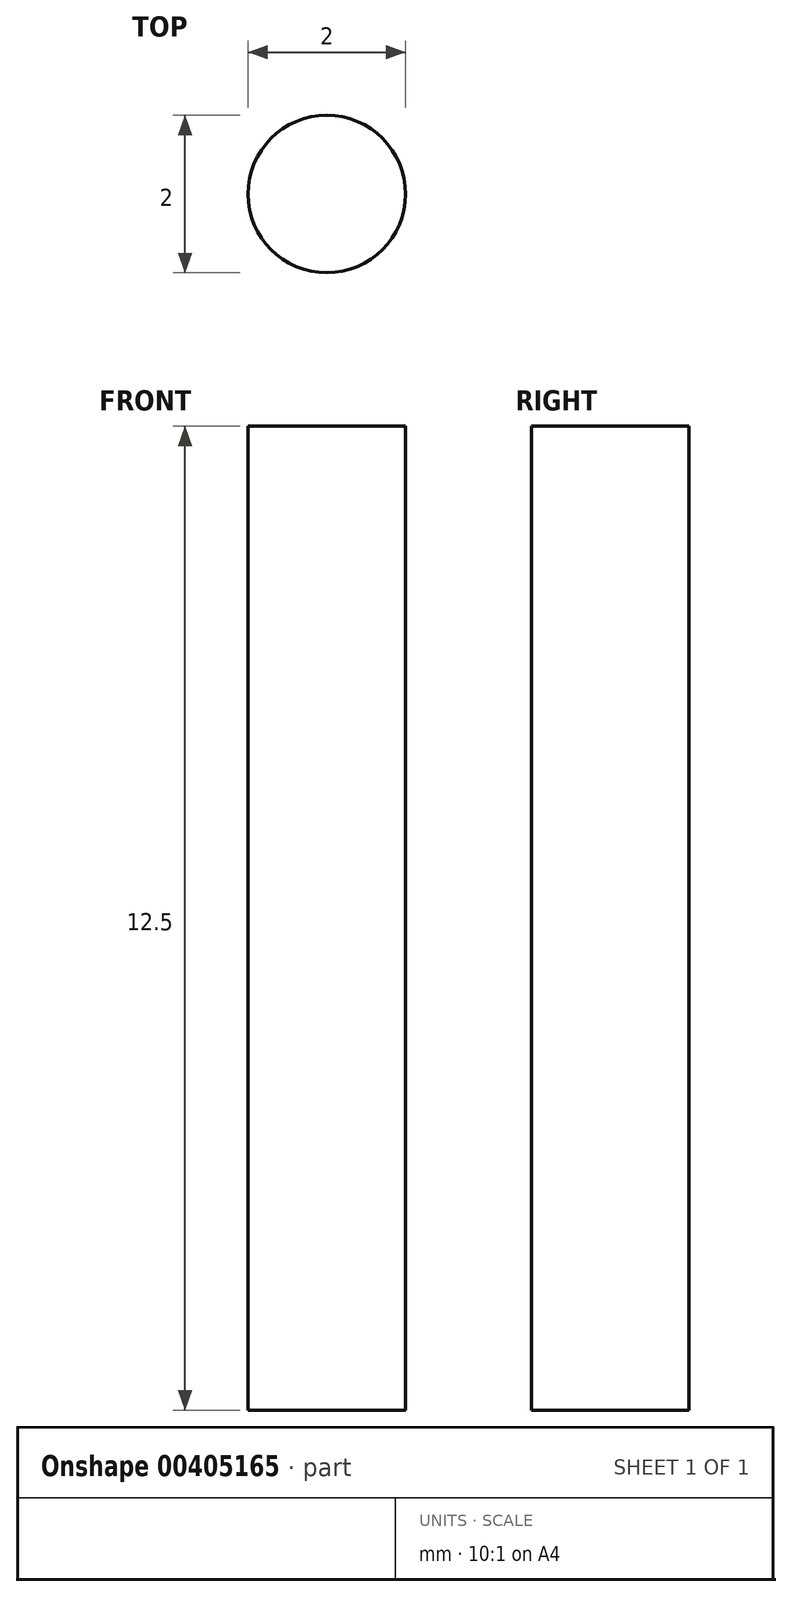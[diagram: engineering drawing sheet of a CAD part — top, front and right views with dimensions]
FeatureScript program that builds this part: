
annotation { "Feature Type Name" : "Feature", "Feature Type Description" : "" }
export const myFeature = defineFeature(function(context is Context, id is Id, definition is map)
    precondition{}
    {
        {
            var Q0;
            Q0=qCreatedBy(makeId("Top.planeOp"),FACE);
            var sketch = newSketch(context, id + "F0", { "sketchPlane" : qUnion([Q0])});
            skCircle(sketch, "E0", {"center": v(0, 0) * mm, "radius": 1 * mm});
            skSolve(sketch);
        }
        {
            var Q0;
            Q0 = qSketchRegion(id + "F0", true);
            extrude(context, id + "F1", {"entities" : qUnion([Q0]), "depth" : 12.5 * mm});
        }
    });
